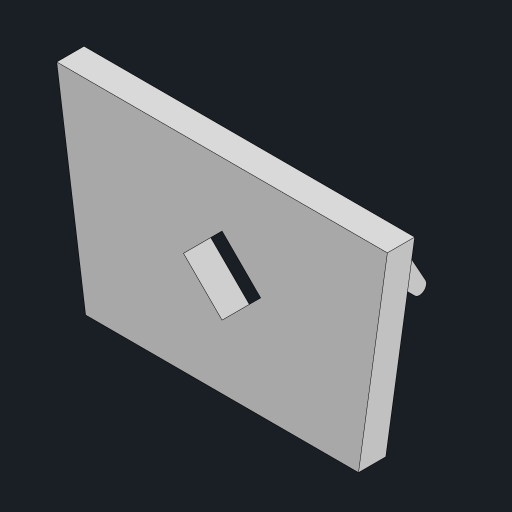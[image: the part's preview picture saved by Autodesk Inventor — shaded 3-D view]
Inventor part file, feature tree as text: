
AUTODESK INVENTOR PART (.ipt)
format: ipt  version: 2023 (Build 270158000, 158)  size: 140,800 bytes
history: native  units: mm
features: other x2, extrude x2, fillet x2, sketch x2, mirror x1, projected_geometry x1
ambient origin geometry x8: Origin, YZ Plane, XZ Plane, XY Plane, X Axis, Y Axis, Z Axis, Center Point
bodies: Body1 (feature_tree)
feature tree (10):
  other  "ソリッド1"
  extrude  "押し出し1"  Depth=2.0mm TaperAngle=0.0deg
  other  "作業平面1"
  extrude  "押し出し3"  Depth=24.229759mm
  fillet  "フィレット1"  Radius=20.0mm
  fillet  "フィレット2"  Radius=15.0mm
  mirror  "ミラー2"
  sketch  "スケッチ1"
  sketch  "スケッチ3"
  projected_geometry  "投影ループ2"
